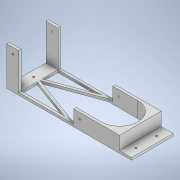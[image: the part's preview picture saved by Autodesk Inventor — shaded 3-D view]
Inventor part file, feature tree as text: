
AUTODESK INVENTOR PART (.ipt)
format: ipt  version: 2020 (Build 240168000, 168)  size: 228,352 bytes
history: native  units: mm
features: sketch x5, other x3, extrude x3, hole x2, mirror x1
ambient origin geometry x8: Origin, YZ Plane, XZ Plane, XY Plane, X Axis, Y Axis, Z Axis, Center Point
bodies: Body1 (feature_tree)
feature tree (14):
  other  "Твердое тело1"
  extrude  "Выдавливание1"  Depth=103.5mm
  extrude  "Выдавливание2"  Depth=10.0mm
  extrude  "Выдавливание3"  Depth=10.0mm
  hole  "Отверстие1"  [1 undecoded]
  hole  "Отверстие2"  [1 undecoded]
  mirror  "Зеркальное отражение1"
  sketch  "Эскиз1"
  sketch  "Эскиз2"
  sketch  "Эскиз3"
  sketch  "Эскиз4"
  sketch  "Эскиз5"
  other  "Проецирование ребер1"
  other  "Проецирование ребер2"
note: 2 required parameter values undecoded (feature->parameter linkage not recoverable at this tier; creation-order binding heuristic only, values carry confidence <= 0.55)
